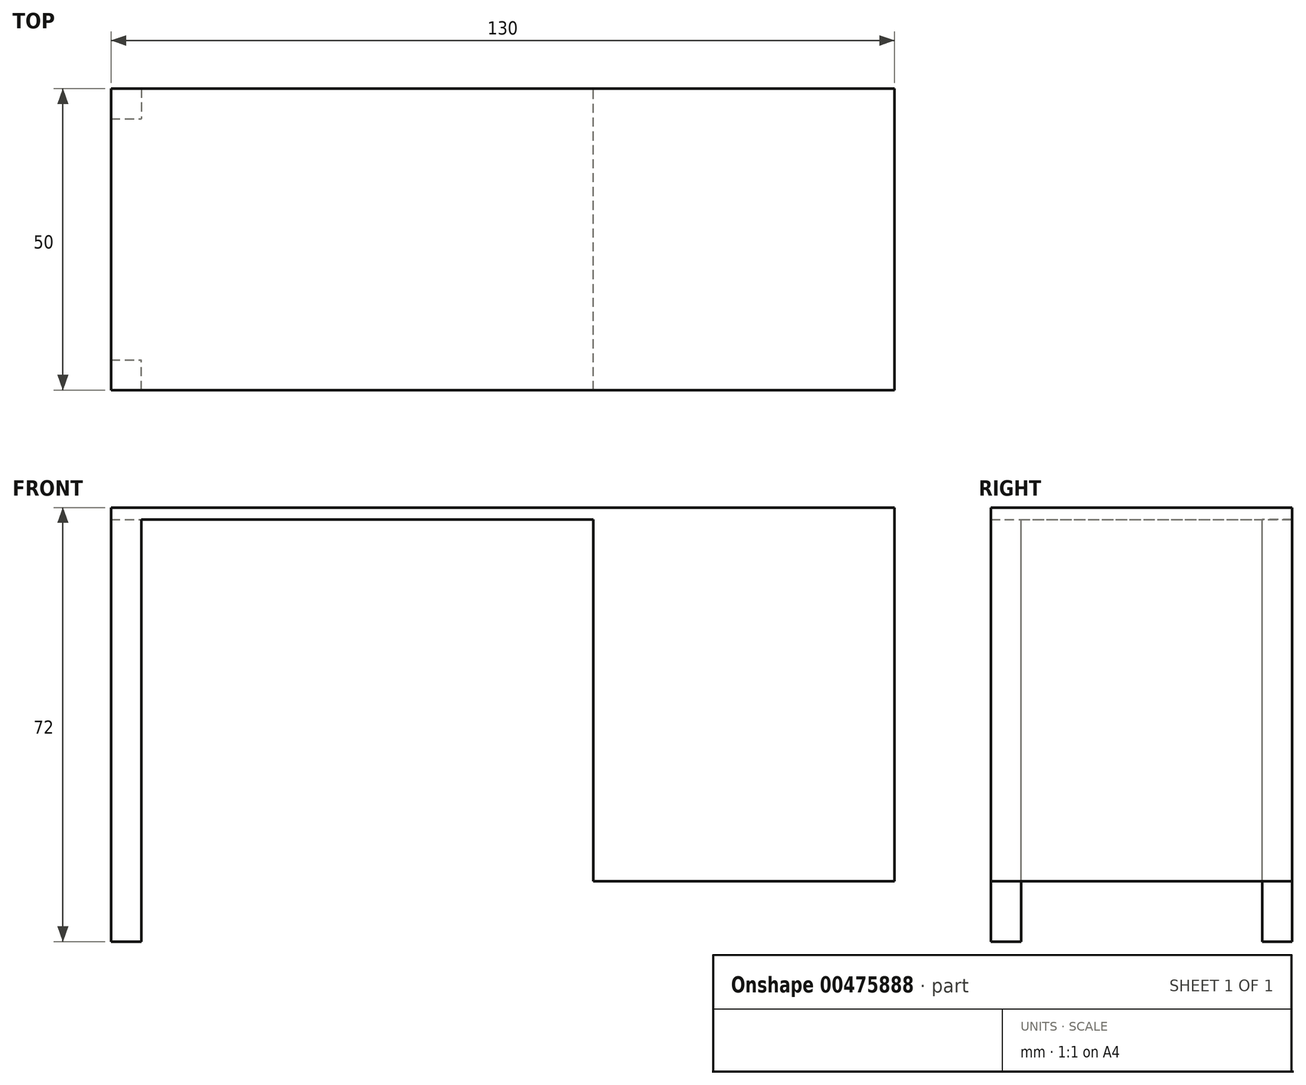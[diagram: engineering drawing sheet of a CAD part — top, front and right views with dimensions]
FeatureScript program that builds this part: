
annotation { "Feature Type Name" : "Feature", "Feature Type Description" : "" }
export const myFeature = defineFeature(function(context is Context, id is Id, definition is map)
    precondition{}
    {
        {
            var Q0;
            Q0=qCreatedBy(makeId("Top.planeOp"),FACE);
            var sketch = newSketch(context, id + "F0", { "sketchPlane" : qUnion([Q0])});
            skLineSegment(sketch, "E0.bottom", {"start": v(65, -25) * mm, "end": v(-65, -25) * mm});
            skLineSegment(sketch, "E0.top", {"start": v(65, 25) * mm, "end": v(-65, 25) * mm});
            skLineSegment(sketch, "E0.left", {"start": v(65, -25) * mm, "end": v(65, 25) * mm});
            skLineSegment(sketch, "E0.right", {"start": v(-65, -25) * mm, "end": v(-65, 25) * mm});
            skPoint(sketch, "E0.middle", {"position": v(0, 0) * mm});
            skSolve(sketch);
        }
        {
            var Q0;
            Q0 = qSketchRegion(id + "F0", true);
            extrude(context, id + "F1", {"entities" : qUnion([Q0]), "depth" : 2 * mm});
        }
        {
            var Q0;
            Q0=makeQuery(id+"F1.opExtrude","CAP_FACE",FACE,{"disambiguationData":[OSD([sQuery(id+"F0.wireOp",EDGE,"E0.bottom"),sQuery(id+"F0.wireOp",EDGE,"E0.top"),sQuery(id+"F0.wireOp",EDGE,"E0.left"),sQuery(id+"F0.wireOp",EDGE,"E0.right")])],"isStart":true});
            var sketch = newSketch(context, id + "F2", { "sketchPlane" : qUnion([Q0])});
            skLineSegment(sketch, "E1.bottom", {"start": v(65, 25) * mm, "end": v(15, 25) * mm});
            skLineSegment(sketch, "E1.top", {"start": v(65, -25) * mm, "end": v(15, -25) * mm});
            skLineSegment(sketch, "E1.left", {"start": v(65, 25) * mm, "end": v(65, -25) * mm});
            skLineSegment(sketch, "E1.right", {"start": v(15, 25) * mm, "end": v(15, -25) * mm});
            skSolve(sketch);
        }
        {
            var Q0;
            Q0 = qSketchRegion(id + "F2", true);
            extrude(context, id + "F3", {"entities" : qUnion([Q0]), "operationType" : NewBodyOperationType.ADD, "depth" : 60 * mm});
        }
        {
            var Q0;
            Q0=makeQuery(id+"F1.opExtrude","CAP_FACE",FACE,{"disambiguationData":[OSD([sQuery(id+"F0.wireOp",EDGE,"E0.bottom"),sQuery(id+"F0.wireOp",EDGE,"E0.top"),sQuery(id+"F0.wireOp",EDGE,"E0.left"),sQuery(id+"F0.wireOp",EDGE,"E0.right")])],"isStart":true});
            var sketch = newSketch(context, id + "F4", { "sketchPlane" : qUnion([Q0])});
            skLineSegment(sketch, "E2.bottom", {"start": v(-65, 25) * mm, "end": v(-60, 25) * mm});
            skLineSegment(sketch, "E2.top", {"start": v(-65, 20) * mm, "end": v(-60, 20) * mm});
            skLineSegment(sketch, "E2.left", {"start": v(-65, 25) * mm, "end": v(-65, 20) * mm});
            skLineSegment(sketch, "E2.right", {"start": v(-60, 25) * mm, "end": v(-60, 20) * mm});
            skLineSegment(sketch, "E3.MirrorCS", {"start": v(-65, -20) * mm, "end": v(-60, -20) * mm});
            skLineSegment(sketch, "E4.MirrorCS", {"start": v(-65, -25) * mm, "end": v(-65, -20) * mm});
            skLineSegment(sketch, "E5.MirrorCS", {"start": v(-65, -25) * mm, "end": v(-60, -25) * mm});
            skLineSegment(sketch, "E6.MirrorCS", {"start": v(-60, -25) * mm, "end": v(-60, -20) * mm});
            skSolve(sketch);
        }
        {
            var Q0;
            Q0 = qSketchRegion(id + "F4", true);
            extrude(context, id + "F5", {"entities" : qUnion([Q0]), "operationType" : NewBodyOperationType.ADD, "depth" : 70 * mm});
        }
    });
